# Revit family: Montageschiene 45-120-3,0 D  6m fsv Langloch 2D
name_source: partatom
category: HLS-Bauteile
units: mm (PartAtom-declared; Revit-internal decimal feet)

## family parameters
Arbeitsebenenbasiert = Ja
Beim Laden mit Abzugskörper schneiden = Nein
Bemaßung runder Anschluss = Durchmesser verwenden
Beschriftungsausrichtung beibehalten = Nein
Gemeinsam genutzt = Ja
Immer vertikal = Nein
Raumberechnungspunkt = Nein
Teiletyp = Normal

## types (1)
- C-Profil 45-120-3,0 D  L=6000 fsv
    Abmessung = 45/120/3.0 mm
    Artikelnummer = 0810833
    Breite = 45 mm  [stored 0.147638 ft]
    Bund = 120 m
    EAN = 4250928419491
    Erweiterung Langloch = 18.0 mm
    Fabrikat = MEFA
    Firma = MEFA Befestigungs- und Montagesysteme GmbH
    Fläche (schwächster Profilquerschnitt) = 0 m²
    Gewicht = 8,63 kg
    Höhe = 120 mm
    Kurztext1 = Montageschiene C-Profil doppelt
    Kurztext2 = 45 / 120 / 3 mm L= 6 m fsv
    Langloch = 14.0 x 45.0 mm
    Lochdurchmesser = 18.00 mm
    Länge = 6000 mm  [stored 19.685 ft]
    Material = Stahl
    Materialname = S235
    Mengeneinheit = m
    Oberflaeche = feuerstückverzinkt
    Profil = Doppel-C-Profil
    Profiltyp = 45/120
    Schlitzbreite = 22 mm
    Schwerpunktabstand eo = 6.00 cm
    Schwerpunktabstand eu = 6.00 cm
    Schwerpunktabstand ez = 2.25 cm
    Streckgrenze = 235 N/mm²
    Stärke = 3 mm  [stored 0.00984252 ft]
    Torsionswiderstandsmoment Wt = cm³
    Trägheitsradius iy = 3.64 cm
    Trägheitsradius iz = 1.95 cm
    Vorgabe-Ansicht = 1219 mm
    Widerstandsmoment Wy = 19.96 cm³
    Widerstandsmoment Wz = 15.25 cm³
    vpe = 24

note: [stored X ft] marks values corroborated as IEEE doubles in the binary element streams (Revit-internal decimal feet)
